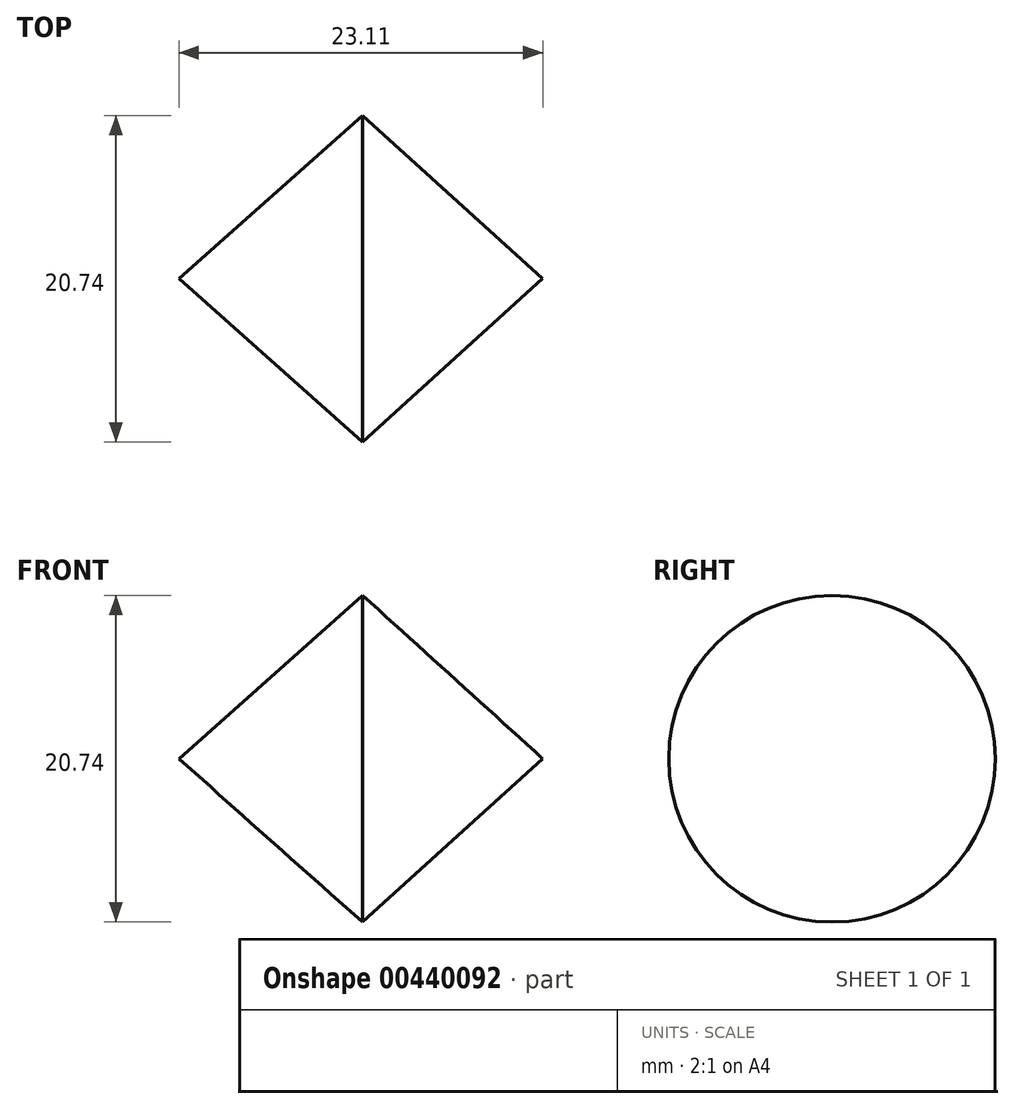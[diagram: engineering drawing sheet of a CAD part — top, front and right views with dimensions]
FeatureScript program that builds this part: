
annotation { "Feature Type Name" : "Feature", "Feature Type Description" : "" }
export const myFeature = defineFeature(function(context is Context, id is Id, definition is map)
    precondition{}
    {
        {
            var Q0;
            Q0=qCreatedBy(makeId("Front.planeOp"),FACE);
            var sketch = newSketch(context, id + "F0", { "sketchPlane" : qUnion([Q0])});
            skLineSegment(sketch, "E0", {"start": v(0, 0) * mm, "end": v(11.44, 0) * mm, "construction": true});
            skLineSegment(sketch, "E1", {"start": v(0, 0) * mm, "end": v(-11.67, 0) * mm, "construction": true});
            skLineSegment(sketch, "E2", {"start": v(-11.67, 0) * mm, "end": v(0, 10.37) * mm});
            skLineSegment(sketch, "E3", {"start": v(0, 10.37) * mm, "end": v(11.44, 0) * mm});
            skSolve(sketch);
        }
        {
            var Q0;
            Q0=sQuery(id+"F0.wireOp",EDGE,"E2");
            var Q1;
            Q1=sQuery(id+"F0.wireOp",EDGE,"E3");
            var Q2;
            Q2=sQuery(id+"F0.wireOp",EDGE,"E0");
            revolve(context, id + "F1", {"bodyType" : ToolBodyType.SURFACE, "surfaceEntities" : qUnion([Q0, Q1]), "axis" : qUnion([Q2]), "revolveType" : RevolveType.FULL});
        }
    });
